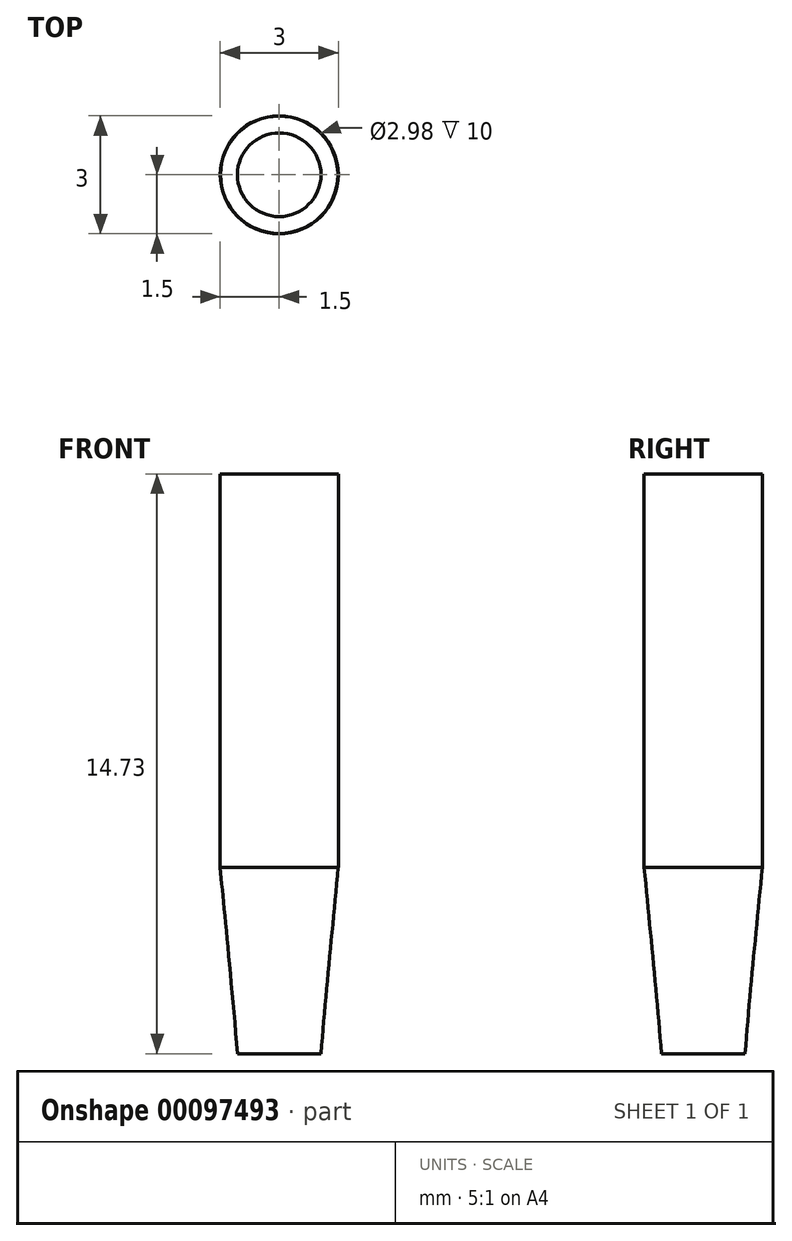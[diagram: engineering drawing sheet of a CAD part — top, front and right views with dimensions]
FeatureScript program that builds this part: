
annotation { "Feature Type Name" : "Feature", "Feature Type Description" : "" }
export const myFeature = defineFeature(function(context is Context, id is Id, definition is map)
    precondition{}
    {
        {
            var Q0;
            Q0=qCreatedBy(makeId("Front.planeOp"),FACE);
            var sketch = newSketch(context, id + "F0", { "sketchPlane" : qUnion([Q0])});
            skLineSegment(sketch, "E0", {"start": v(0, 0) * mm, "end": v(0, 80) * mm, "construction": true});
            skLineSegment(sketch, "E1", {"start": v(0, 80) * mm, "end": v(1.49, 80) * mm, "construction": true});
            skLineSegment(sketch, "E2", {"start": v(1.49, 80) * mm, "end": v(1.5, 70) * mm});
            skPoint(sketch, "E3", {"position": v(1.49, 60) * mm});
            skPoint(sketch, "E4", {"position": v(1.5, 45) * mm});
            skPoint(sketch, "E5", {"position": v(1.5, 30) * mm});
            skLineSegment(sketch, "E6", {"start": v(1.49, 70) * mm, "end": v(1.5, 0) * mm, "construction": true});
            skPoint(sketch, "E7", {"position": v(0.74, 60) * mm});
            skPoint(sketch, "E8", {"position": v(0.6, 45) * mm});
            skPoint(sketch, "E9", {"position": v(0.5, 30) * mm});
            skPoint(sketch, "E10", {"position": v(0.5, 0) * mm});
            skFitSpline(sketch, "E11", {"points": [v(1.49, 70) * mm, v(0.74, 60) * mm, v(0.6, 45) * mm, v(0.5, 30) * mm, v(0.5, 0) * mm], "startDerivative": vector(-4.66, -48.57) * mm, "endDerivative": vector(0.19, -98.2) * mm});
            skArc(sketch, "E12", {"start": v(0, -0.5) * mm, "mid": v(0.35, -0.35) * mm, "end": v(0.5, 0) * mm});
            skLineSegment(sketch, "E13", {"start": v(0, 0) * mm, "end": v(0, -0.5) * mm, "construction": true});
            skLineSegment(sketch, "E14.0", {"start": v(1.5, 80) * mm, "end": v(1.5, 70) * mm});
            skLineSegment(sketch, "E15", {"start": v(1.49, 80) * mm, "end": v(1.5, 80) * mm});
            skFitSpline(sketch, "E16.0", {"points": [v(1.5, 70) * mm, v(1.4, 68.99) * mm, v(1.2, 66.96) * mm, v(0.95, 63.8) * mm, v(0.75, 60.4) * mm, v(0.64, 56.6) * mm, v(0.6, 52.56) * mm, v(0.6, 49.15) * mm, v(0.6, 46.46) * mm, v(0.6, 43.84) * mm, v(0.58, 40.7) * mm, v(0.55, 36.93) * mm, v(0.52, 33.6) * mm, v(0.5, 30.71) * mm, v(0.5, 28.4) * mm, v(0.48, 25.96) * mm, v(0.48, 22.53) * mm, v(0.47, 17.97) * mm, v(0.48, 12.16) * mm, v(0.49, 6.14) * mm, v(0.5, 2.05) * mm, v(0.5, 0) * mm]});
            skLineSegment(sketch, "E17", {"start": v(0, -0.5) * mm, "end": v(0, -0.5) * mm});
            skLineSegment(sketch, "E18", {"start": v(1.5, 70) * mm, "end": v(1.5, 70) * mm});
            skSolve(sketch);
        }
        {
            var Q0;
            Q0=makeQuery(id+"F0.imprint","IMPRINT",FACE,{"disambiguationData":[TD([[makeQuery(id+"F0.imprint","IMPRINT",EDGE,{"derivedFrom":sQuery(id+"F0.wireOp",EDGE,"E2")}),1.0]])]});
            var Q1;
            Q1=sQuery(id+"F0.wireOp",EDGE,"E0");
            revolve(context, id + "F1", {"entities" : qUnion([Q0]), "axis" : qUnion([Q1]), "revolveType" : RevolveType.FULL});
        }
    });
